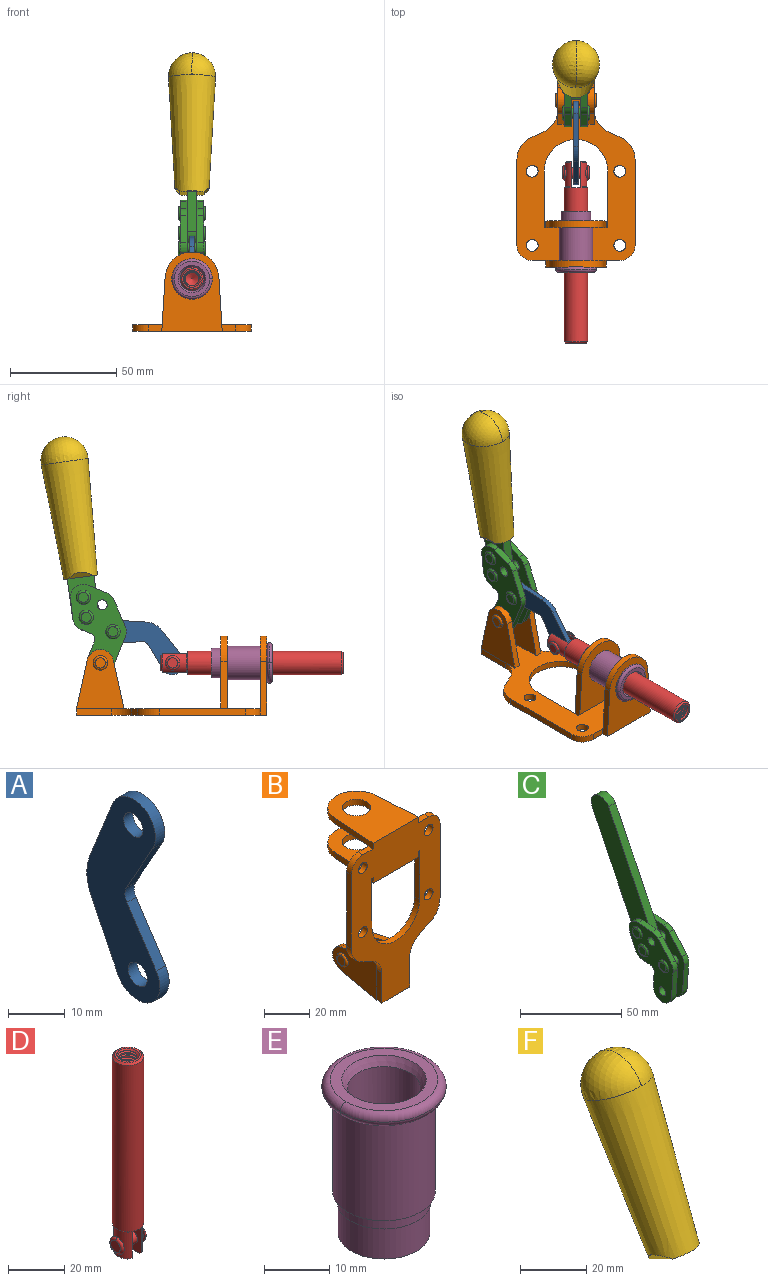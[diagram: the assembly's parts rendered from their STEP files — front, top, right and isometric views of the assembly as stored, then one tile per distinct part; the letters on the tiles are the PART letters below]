
ASSEMBLY  parts=6 mates=6
PART A: 12 faces, bbox 2.3x18.2x42.8 mm
  f0: cylinder r=2.4mm len=4.8mm, axis (1,0,0), area 34.9mm2, adj f4,f11
  f1: cylinder r=10.41mm len=8.47mm, axis (1,0,0), area 20.2mm2, adj f4,f9,f10,f11
  f2: cylinder r=3.05mm len=3.16mm, axis (1,0,0), area 7.7mm2, adj f4,f6,f7,f11
  f3: cylinder r=2.4mm len=4.8mm, axis (1,0,0), area 34.9mm2, adj f4,f11
  f4: plane 42.81x18.23mm, normal (-1,0,0), area 414.1mm2, adj f0,f1,f2,f3,f5,f6,f7,f8
  f5: cylinder r=5.54mm len=10.67mm, axis (1,0,0), area 41.8mm2, adj f4,f6,f10,f11
  f6: plane 11.66x6.53mm, normal (0,-0.87,-0.49), area 30.9mm2, adj f2,f4,f5,f11
  f7: plane 11.17x7.33mm, normal (0,-0.84,0.55), area 30.9mm2, adj f2,f4,f8,f11
  f8: cylinder r=5.54mm len=10.51mm, axis (1,0,0), area 41.8mm2, adj f4,f7,f9,f11
  f9: plane 13.67x6.67mm, normal (0,0.9,-0.44), area 35.1mm2, adj f1,f4,f8,f11
  f10: plane 14.1x5.7mm, normal (0,0.93,0.37), area 35.1mm2, adj f1,f4,f5,f11
  f11: plane 42.81x18.23mm, normal (1,0,0), area 414.1mm2, adj f0,f1,f2,f3,f5,f6,f7,f8
PART B: 55 faces, bbox 55.7x37.4x89.8 mm
  f0: torus R=2.41mm, axis (-1,0,0), area 15mm2, adj f11,f15,f25
  f1: torus R=2.41mm, axis (-1,0,0), area 15mm2, adj f10,f12,f22
  f2: cylinder r=2.78mm len=5.56mm, axis (0,-1,0), area 54.2mm2, adj f30,f54
  f3: cylinder r=14.99mm len=29.97mm, axis (0,-1,0), area 145.9mm2, adj f30,f49,f53,f54
  f4: cylinder r=2.78mm len=5.56mm, axis (0,-1,0), area 54.2mm2, adj f30,f54
  f5: cylinder r=2.78mm len=5.56mm, axis (0,-1,0), area 54.2mm2, adj f30,f54
  f6: cylinder r=2.78mm len=5.56mm, axis (0,-1,0), area 54.2mm2, adj f30,f54
  f7: cylinder r=6.35mm len=12.7mm, axis (0,0,1), area 123.6mm2, adj f27,f51
  f8: cylinder r=6.35mm len=12.7mm, axis (0,0,-1), area 124.7mm2, adj f21,f35
  f9: cylinder r=2.41mm len=11.18mm, axis (-1,0,0), area 169.4mm2, adj f16,f19
  f10: plane 4.83x4.83mm, normal (1,0,0), area 18.3mm2, adj f1,f12
  f11: plane 4.83x4.83mm, normal (-1,0,0), area 18.3mm2, adj f0,f15
  f12: torus R=2.41mm, axis (-1,0,0), area 15mm2, adj f1,f10,f22
  f13: cylinder r=6.35mm len=12.41mm, axis (1,0,0), area 53.4mm2, adj f18,f19,f22,f23
  f14: cylinder r=6.35mm len=12.41mm, axis (-1,0,0), area 53.4mm2, adj f16,f17,f24,f25
  f15: torus R=2.41mm, axis (-1,0,0), area 15mm2, adj f0,f11,f25
  f16: plane 27.86x22.35mm, normal (1,0,0), area 425.4mm2, adj f9,f14,f17,f24,f30
  f17: plane 22.86x4.97mm, normal (0,0.21,0.98), area 72.5mm2, adj f14,f16,f25,f30
  f18: plane 22.86x4.97mm, normal (0,0.21,0.98), area 72.5mm2, adj f13,f19,f22,f30
  f19: plane 27.86x22.35mm, normal (-1,0,0), area 425.4mm2, adj f9,f13,f18,f23,f30
  f20: cylinder r=12.7mm len=25.35mm, axis (0,0,-1), area 119.8mm2, adj f21,f34,f35,f36
  f21: plane 34.21x28.07mm, normal (0,0,-1), area 702.4mm2, adj f8,f20,f30,f34,f36
  f22: plane 27.96x22.45mm, normal (1,0,0), area 407.2mm2, adj f1,f12,f13,f18,f23,f30,f42,f43
  f23: plane 22.86x4.97mm, normal (0,0.21,-0.98), area 72.5mm2, adj f13,f19,f22,f44
  f24: plane 22.86x4.97mm, normal (0,0.21,-0.98), area 72.5mm2, adj f14,f16,f25,f44
  f25: plane 27.86x22.35mm, normal (-1,0,0), area 407.1mm2, adj f0,f14,f15,f17,f24,f30,f45,f46
  f26: plane 3.1x0.95mm, normal (0,0,-1), area 2.7mm2, adj f30,f49,f50,f54
  f27: plane 34.21x28.07mm, normal (0,0,1), area 702.4mm2, adj f7,f28,f30,f50,f52
  f28: cylinder r=12.7mm len=25.35mm, axis (0,0,1), area 118.8mm2, adj f27,f50,f51,f52
  f29: plane 3.1x0.95mm, normal (0,0,-1), area 2.7mm2, adj f30,f52,f53,f54
  f30: plane 86.54x55.63mm, normal (0,1,0), area 2362.9mm2, adj f2,f3,f4,f5,f6,f16,f17,f18
  f31: plane 40.56x3.1mm, normal (-1,0,0), area 125.7mm2, adj f30,f32,f48,f54
  f32: cylinder r=7.11mm len=7.11mm, axis (0,-1,0), area 34.6mm2, adj f30,f31,f33,f54
  f33: plane 6.67x3.1mm, normal (0,0,1), area 20.4mm2, adj f30,f32,f34,f54
  f34: plane 25.39x3.13mm, normal (-1,0.06,0), area 79.5mm2, adj f20,f21,f33,f35,f54
  f35: plane 37.31x28.45mm, normal (0,0,1), area 789.9mm2, adj f8,f20,f34,f36,f54
  f36: plane 25.39x3.13mm, normal (1,0.06,0), area 79.5mm2, adj f20,f21,f35,f37,f54
  f37: plane 6.67x3.1mm, normal (0,0,1), area 20.4mm2, adj f30,f36,f38,f54
  f38: cylinder r=7.11mm len=7.11mm, axis (0,-1,0), area 34.6mm2, adj f30,f37,f39,f54
  f39: plane 40.56x3.1mm, normal (1,0,0), area 125.7mm2, adj f30,f38,f40,f54
  f40: cylinder r=11.18mm len=10.16mm, axis (0,-1,0), area 39.5mm2, adj f30,f39,f41,f54
  f41: plane 6.09x3.1mm, normal (0.42,0,-0.91), area 20.8mm2, adj f30,f40,f42,f54
  f42: cylinder r=11.18mm len=9.41mm, axis (0,-1,0), area 37.2mm2, adj f22,f30,f41,f43,f54
  f43: plane 16.5x3.1mm, normal (1,0,0), area 51.1mm2, adj f22,f42,f44,f54
  f44: plane 17.37x3.1mm, normal (0,0,-1), area 53.8mm2, adj f23,f24,f30,f43,f45,f54
  f45: plane 16.5x3.1mm, normal (-1,0,0), area 51.1mm2, adj f25,f44,f46,f54
  f46: cylinder r=11.18mm len=9.41mm, axis (0,-1,0), area 37.2mm2, adj f25,f30,f45,f47,f54
  f47: plane 6.09x3.1mm, normal (-0.42,0,-0.91), area 20.8mm2, adj f30,f46,f48,f54
  f48: cylinder r=11.18mm len=10.16mm, axis (0,-1,0), area 39.5mm2, adj f30,f31,f47,f54
  f49: plane 26.54x3.1mm, normal (-1,0,0), area 82.3mm2, adj f3,f26,f30,f54
  f50: plane 25.39x3.1mm, normal (1,0.06,0), area 78.8mm2, adj f26,f27,f28,f51,f54
  f51: plane 37.31x28.45mm, normal (0,0,-1), area 789.9mm2, adj f7,f28,f50,f52,f54
  f52: plane 25.39x3.1mm, normal (-1,0.06,0), area 78.8mm2, adj f27,f28,f29,f51,f54
  f53: plane 26.54x3.1mm, normal (1,0,0), area 82.3mm2, adj f3,f29,f30,f54
  f54: plane 89.66x55.63mm, normal (0,-1,0), area 2678.5mm2, adj f2,f3,f4,f5,f6,f26,f29,f31
PART C: 59 faces, bbox 12.9x60.2x99.6 mm
  f0: torus R=2.39mm, axis (-1,0,0), area 14.9mm2, adj f20,f43,f51
  f1: torus R=2.39mm, axis (-1,0,0), area 14.9mm2, adj f19,f42,f51
  f2: torus R=2.39mm, axis (-1,0,0), area 14.9mm2, adj f18,f35,f51
  f3: torus R=2.39mm, axis (-1,0,0), area 14.9mm2, adj f14,f17,f23
  f4: torus R=2.39mm, axis (-1,0,0), area 14.9mm2, adj f13,f16,f23
  f5: torus R=2.39mm, axis (-1,0,0), area 14.9mm2, adj f12,f15,f23
  f6: cylinder r=2.39mm len=4.78mm, axis (1,0,0), area 46.5mm2, adj f48,f50,f51
  f7: cylinder r=2.39mm len=4.78mm, axis (1,0,0), area 46.5mm2, adj f50,f51
  f8: cylinder r=6.35mm len=12.68mm, axis (1,0,0), area 61.8mm2, adj f38,f39,f50,f51
  f9: cylinder r=2.39mm len=4.78mm, axis (-1,0,0), area 70.5mm2, adj f46,f50
  f10: cylinder r=2.39mm len=4.78mm, axis (-1,0,0), area 46.5mm2, adj f23,f45,f46
  f11: cylinder r=2.39mm len=4.78mm, axis (-1,0,0), area 46.5mm2, adj f23,f46
  f12: plane 4.78x4.78mm, normal (1,0,0), area 17.9mm2, adj f5,f15
  f13: plane 4.78x4.78mm, normal (1,0,0), area 17.9mm2, adj f4,f16
  f14: plane 4.78x4.78mm, normal (1,0,0), area 17.9mm2, adj f3,f17
  f15: torus R=2.39mm, axis (-1,0,0), area 14.9mm2, adj f5,f12,f23
  f16: torus R=2.39mm, axis (-1,0,0), area 14.9mm2, adj f4,f13,f23
  f17: torus R=2.39mm, axis (-1,0,0), area 14.9mm2, adj f3,f14,f23
  f18: plane 4.78x4.78mm, normal (-1,0,0), area 17.9mm2, adj f2,f35
  f19: plane 4.78x4.78mm, normal (-1,0,0), area 17.9mm2, adj f1,f42
  f20: plane 4.78x4.78mm, normal (-1,0,0), area 17.9mm2, adj f0,f43
  f21: plane 2.26x0.2mm, normal (1,0,0), area 0.2mm2, adj f31,f44
  f22: plane 2.26x0.2mm, normal (-1,0,0), area 0.2mm2, adj f41,f44
  f23: plane 39.37x30.77mm, normal (1,0,0), area 565.5mm2, adj f3,f4,f5,f10,f11,f15,f16,f17
  f24: cylinder r=6.1mm len=4.15mm, axis (-1,0,0), area 14.7mm2, adj f23,f25,f32,f46
  f25: plane 10.25x9.01mm, normal (0,-0.75,0.66), area 42.3mm2, adj f23,f24,f26,f46
  f26: cylinder r=6.35mm len=4.64mm, axis (-1,0,0), area 15.6mm2, adj f23,f25,f27,f46
  f27: plane 15.84x3.1mm, normal (0,-1,-0.07), area 49.2mm2, adj f23,f26,f28,f46
  f28: cylinder r=6.35mm len=12.68mm, axis (-1,0,0), area 61.8mm2, adj f23,f27,f29,f46
  f29: plane 8.11x3.1mm, normal (0,1,0.07), area 25.2mm2, adj f23,f28,f30,f46
  f30: cylinder r=3.05mm len=3.25mm, axis (-1,0,0), area 14.8mm2, adj f23,f29,f31,f46
  f31: plane 5.99x3.1mm, normal (0,0.07,-1), area 18.6mm2, adj f21,f23,f30,f44,f46
  f32: plane 9.5x3.1mm, normal (0,-0.07,1), area 29.5mm2, adj f23,f24,f33,f46,f47
  f33: cylinder r=6.1mm len=8.63mm, axis (-1,0,0), area 39.1mm2, adj f23,f32,f34,f47
  f34: plane 8.65x3.96mm, normal (0,0.91,-0.42), area 29.5mm2, adj f23,f33,f44,f47
  f35: torus R=2.39mm, axis (-1,0,0), area 14.9mm2, adj f2,f18,f51
  f36: plane 10.25x9.01mm, normal (0,-0.75,0.66), area 42.3mm2, adj f37,f49,f50,f51
  f37: cylinder r=6.35mm len=4.64mm, axis (1,0,0), area 15.6mm2, adj f36,f38,f50,f51
  f38: plane 15.84x3.1mm, normal (0,-1,-0.07), area 49.2mm2, adj f8,f37,f50,f51
  f39: plane 8.11x3.1mm, normal (0,1,0.07), area 25.2mm2, adj f8,f40,f50,f51
  f40: cylinder r=3.05mm len=3.25mm, axis (1,0,0), area 14.8mm2, adj f39,f41,f50,f51
  f41: plane 5.99x3.1mm, normal (0,0.07,-1), area 18.6mm2, adj f22,f40,f44,f50,f51
  f42: torus R=2.39mm, axis (-1,0,0), area 14.9mm2, adj f1,f19,f51
  f43: torus R=2.39mm, axis (-1,0,0), area 14.9mm2, adj f0,f20,f51
  f44: cylinder r=6.35mm len=12.12mm, axis (-1,0,0), area 128.9mm2, adj f21,f22,f23,f31,f34,f41,f46,f47
  f45: plane 2.65x1.35mm, normal (1,0,0), area 1mm2, adj f10,f55
  f46: plane 39.08x20.42mm, normal (-1,0,0), area 412.5mm2, adj f9,f10,f11,f24,f25,f26,f27,f28
  f47: plane 77.62x39.82mm, normal (1,0,0), area 850mm2, adj f32,f33,f34,f44,f53,f54,f55
  f48: plane 2.65x1.35mm, normal (-1,0,0), area 1mm2, adj f6,f55
  f49: cylinder r=6.1mm len=4.15mm, axis (1,0,0), area 14.7mm2, adj f36,f50,f51,f56
  f50: plane 39.08x20.42mm, normal (1,0,0), area 412.5mm2, adj f6,f7,f8,f9,f36,f37,f38,f39
  f51: plane 39.37x30.77mm, normal (-1,0,0), area 565.5mm2, adj f0,f1,f2,f6,f7,f8,f35,f36
  f52: plane 8.65x3.96mm, normal (0,0.91,-0.42), area 29.5mm2, adj f44,f51,f57,f58
  f53: plane 68.49x33.4mm, normal (0,0.9,-0.44), area 358.1mm2, adj f44,f47,f54,f58
  f54: cylinder r=6.35mm len=12.06mm, axis (1,0,0), area 93.7mm2, adj f47,f53,f55,f58
  f55: plane 68.49x33.4mm, normal (0,-0.9,0.44), area 358.1mm2, adj f44,f45,f46,f47,f48,f50,f54,f58
  f56: plane 9.5x3.1mm, normal (0,-0.07,1), area 29.5mm2, adj f49,f50,f51,f57,f58
  f57: cylinder r=6.1mm len=8.63mm, axis (1,0,0), area 39.1mm2, adj f51,f52,f56,f58
  f58: plane 77.62x39.82mm, normal (-1,0,0), area 850mm2, adj f44,f52,f53,f54,f55,f56,f57
PART D: 48 faces, bbox 12.6x11.1x86.1 mm
  f0: torus R=2.41mm, axis (-1,0,0), area 15mm2, adj f30,f32,f34
  f1: torus R=2.41mm, axis (-1,0,0), area 15mm2, adj f29,f31,f33
  f2: cylinder r=5.54mm len=72.39mm, axis (0,0,1), area 2518.5mm2, adj f3,f4,f42,f43
  f3: cone r=5.54mm half-angle=45deg, axis (0,0,1), area 7.6mm2, adj f2,f5,f41
  f4: cone r=5.54mm half-angle=45deg, axis (0,0,-1), area 34.9mm2, adj f2,f39
  f5: cylinder r=5.08mm len=11.48mm, axis (0,0,1), area 108.3mm2, adj f3,f7,f8,f41
  f6: cylinder r=2.41mm len=4.83mm, axis (-1,0,0), area 71.2mm2, adj f40,f41
  f7: cylinder r=2.41mm len=4.83mm, axis (-1,0,0), area 7.6mm2, adj f5,f34
  f8: cone r=5.08mm half-angle=45deg, axis (0,0,1), area 10.6mm2, adj f5,f37,f41
  f9: cone r=3.98mm half-angle=45deg, axis (0,0,1), area 17.6mm2, adj f27,f39,f45,f46,f47
  f10: cylinder r=2.41mm len=4.83mm, axis (-1,0,0), area 7.6mm2, adj f33,f38
  f11: cylinder r=3.2mm len=6.4mm, axis (0,0,1), area 78.4mm2, adj f12,f28,f44,f45,f47
  f12: cylinder r=3.2mm len=6.4mm, axis (0,0,1), area 10.5mm2, adj f11,f13,f45,f47
  f13: cylinder r=3.2mm len=6.4mm, axis (0,0,1), area 10.5mm2, adj f12,f14,f45,f47
  f14: cylinder r=3.2mm len=6.4mm, axis (0,0,1), area 10.5mm2, adj f13,f15,f45,f47
  f15: cylinder r=3.2mm len=6.4mm, axis (0,0,1), area 10.5mm2, adj f14,f16,f45,f47
  f16: cylinder r=3.2mm len=6.4mm, axis (0,0,1), area 10.5mm2, adj f15,f17,f45,f47
  f17: cylinder r=3.2mm len=6.4mm, axis (0,0,1), area 10.5mm2, adj f16,f18,f45,f47
  f18: cylinder r=3.2mm len=6.4mm, axis (0,0,1), area 10.5mm2, adj f17,f19,f45,f47
  f19: cylinder r=3.2mm len=6.4mm, axis (0,0,1), area 10.5mm2, adj f18,f20,f45,f47
  f20: cylinder r=3.2mm len=6.4mm, axis (0,0,1), area 10.5mm2, adj f19,f21,f45,f47
  f21: cylinder r=3.2mm len=6.4mm, axis (0,0,1), area 10.5mm2, adj f20,f22,f45,f47
  f22: cylinder r=3.2mm len=6.4mm, axis (0,0,1), area 10.5mm2, adj f21,f23,f45,f47
  f23: cylinder r=3.2mm len=6.4mm, axis (0,0,1), area 10.5mm2, adj f22,f24,f45,f47
  f24: cylinder r=3.2mm len=6.4mm, axis (0,0,1), area 10.5mm2, adj f23,f25,f45,f47
  f25: cylinder r=3.2mm len=6.4mm, axis (0,0,1), area 10.5mm2, adj f24,f26,f45,f47
  f26: cylinder r=3.2mm len=6.4mm, axis (0,0,1), area 10.5mm2, adj f25,f27,f45,f47
  f27: cylinder r=3.2mm len=6.4mm, axis (0,0,1), area 7.4mm2, adj f9,f26,f45,f47
  f28: cone r=3.2mm half-angle=60deg, axis (0,0,1), area 37.2mm2, adj f11
  f29: plane 4.83x4.83mm, normal (-1,0,0), area 18.3mm2, adj f1,f31
  f30: plane 4.83x4.83mm, normal (1,0,0), area 18.3mm2, adj f0,f32
  f31: torus R=2.41mm, axis (-1,0,0), area 15mm2, adj f1,f29,f33
  f32: torus R=2.41mm, axis (-1,0,0), area 15mm2, adj f0,f30,f34
  f33: plane 6.83x6.83mm, normal (1,0,0), area 18.3mm2, adj f1,f10,f31
  f34: plane 6.83x6.83mm, normal (-1,0,0), area 18.3mm2, adj f0,f7,f32
  f35: cone r=5.08mm half-angle=45deg, axis (0,0,1), area 10.6mm2, adj f36,f38,f40
  f36: plane 7.25x1.97mm, normal (0,0,-1), area 10mm2, adj f35,f40
  f37: plane 7.25x1.97mm, normal (0,0,-1), area 10mm2, adj f8,f41
  f38: cylinder r=5.08mm len=11.48mm, axis (0,0,1), area 108.3mm2, adj f10,f35,f40,f42
  f39: plane 9.55x9.55mm, normal (0,0,1), area 22mm2, adj f4,f9
  f40: plane 12.76x10.09mm, normal (1,0,0), area 95.7mm2, adj f6,f35,f36,f38,f42,f43
  f41: plane 12.76x10.09mm, normal (-1,0,0), area 95.7mm2, adj f3,f5,f6,f8,f37,f43
  f42: cone r=5.54mm half-angle=45deg, axis (0,0,1), area 7.6mm2, adj f2,f38,f40
  f43: plane 11.07x4.7mm, normal (0,0,-1), area 50.4mm2, adj f2,f40,f41
  f44: plane 0.89x0.62mm, normal (-1,0,0), area 0.3mm2, adj f11,f45,f46,f47
  f45: bspline ~24.8x7.63mm, area 266.6mm2, adj f9,f11,f12,f13,f14,f15,f16,f17
  f46: bspline ~24.87x7.63mm, area 73.6mm2, adj f9,f44,f45,f47
  f47: bspline ~24.98x7.63mm, area 272.5mm2, adj f9,f11,f12,f13,f14,f15,f16,f17
PART E: 15 faces, bbox 20.6x20.6x28.7 mm
  f0: torus R=8.26mm, axis (0,0,1), area 56.8mm2, adj f1,f10,f12
  f1: torus R=8.26mm, axis (0,0,1), area 56.8mm2, adj f0,f6,f13
  f2: cylinder r=5.59mm len=25.91mm, axis (0,0,1), area 909.6mm2, adj f3,f4
  f3: cone r=6.86mm half-angle=45deg, axis (0,0,-1), area 70.2mm2, adj f2,f14
  f4: cone r=6.47mm half-angle=30deg, axis (0,0,1), area 66.7mm2, adj f2,f13
  f5: cylinder r=7.04mm len=14.07mm, axis (0,0,1), area 252.6mm2, adj f11,f14
  f6: torus R=8.26mm, axis (0,0,1), area 56.8mm2, adj f1,f12,f13
  f7: cylinder r=7.16mm len=14.33mm, axis (0,0,1), area 91.5mm2, adj f9,f11
  f8: cylinder r=7.86mm len=18.42mm, axis (0,0,1), area 909.6mm2, adj f9,f10
  f9: plane 15.72x15.72mm, normal (0,0,-1), area 33mm2, adj f7,f8
  f10: plane 16.51x16.51mm, normal (0,0,-1), area 19.9mm2, adj f0,f8,f12
  f11: plane 14.33x14.33mm, normal (0,0,-1), area 5.7mm2, adj f5,f7
  f12: torus R=8.26mm, axis (0,0,1), area 56.8mm2, adj f0,f6,f10
  f13: plane 16.51x16.51mm, normal (0,0,1), area 82.7mm2, adj f1,f4,f6
  f14: plane 14.07x14.07mm, normal (0,0,-1), area 7.8mm2, adj f3,f5
PART F: 11 faces, bbox 22.3x42.6x64.5 mm
  f0: sphere r=11.13mm, area 411.4mm2, adj f1,f8
  f1: cone r=11.11mm half-angle=3.3deg, axis (0,0.44,0.9), area 3251.8mm2, adj f0,f7,f8,f9,f10
  f2: cylinder r=6.16mm len=11.7mm, axis (1,0,0), area 89.5mm2, adj f3,f4,f5,f6
  f3: plane 60.23x36.75mm, normal (-1,0,0), area 763.6mm2, adj f2,f4,f6,f10
  f4: plane 51.37x25.05mm, normal (0,0.9,-0.44), area 264.2mm2, adj f2,f3,f5,f10
  f5: plane 60.23x36.75mm, normal (1,0,0), area 763.6mm2, adj f2,f4,f6,f10
  f6: plane 51.37x25.05mm, normal (0,-0.9,0.44), area 264.2mm2, adj f2,f3,f5,f10
  f7: plane 9.95x5.95mm, normal (0.71,-0.31,-0.64), area 25.8mm2, adj f1,f10
  f8: sphere r=11.13mm, area 411.4mm2, adj f0,f1
  f9: plane 9.95x5.95mm, normal (-0.71,-0.31,-0.64), area 25.8mm2, adj f1,f10
  f10: plane 14.27x11.38mm, normal (0,-0.44,-0.9), area 106.7mm2, adj f1,f3,f4,f5,f6,f7,f9
PLACE A rot(axis=(1,0,0),119.6deg) t=(0,25.14,10.19)mm
PLACE B rot(axis=(1,0,0),90deg) t=(0,1.56,-0.66)mm fixed
PLACE C rot(axis=(1,0,0),18.1deg) t=(0,0.27,46.79)mm
PLACE D rot(axis=(1,0,0),90deg) t=(0,15,-0.66)mm
PLACE E rot(axis=(1,0,0),90deg) t=(0,1.56,-0.66)mm
PLACE F rot(axis=(1,0,0),18.1deg) t=(0,0.27,46.79)mm
MATE slider D.f2 <-> B.f7  axis (0,-1,0) through (0,-43.78,23.96)mm
MATE fastened E.f0 <-> B.f7  axis (0,1,0) through (0,-44.83,23.96)mm
MATE fastened F.f2 <-> C.f54  axis (1,0,0) through (0,50.72,120.96)mm
MATE revolute A.f5 <-> D.f6  axis (1,0,0) through (0,-0.47,23.96)mm
MATE revolute A.f3 <-> C.f4  axis (1,0,0) through (0,27.67,38.66)mm
MATE revolute C.f7 <-> B.f0  axis (-1,0,0) through (0,33.65,23.96)mm
